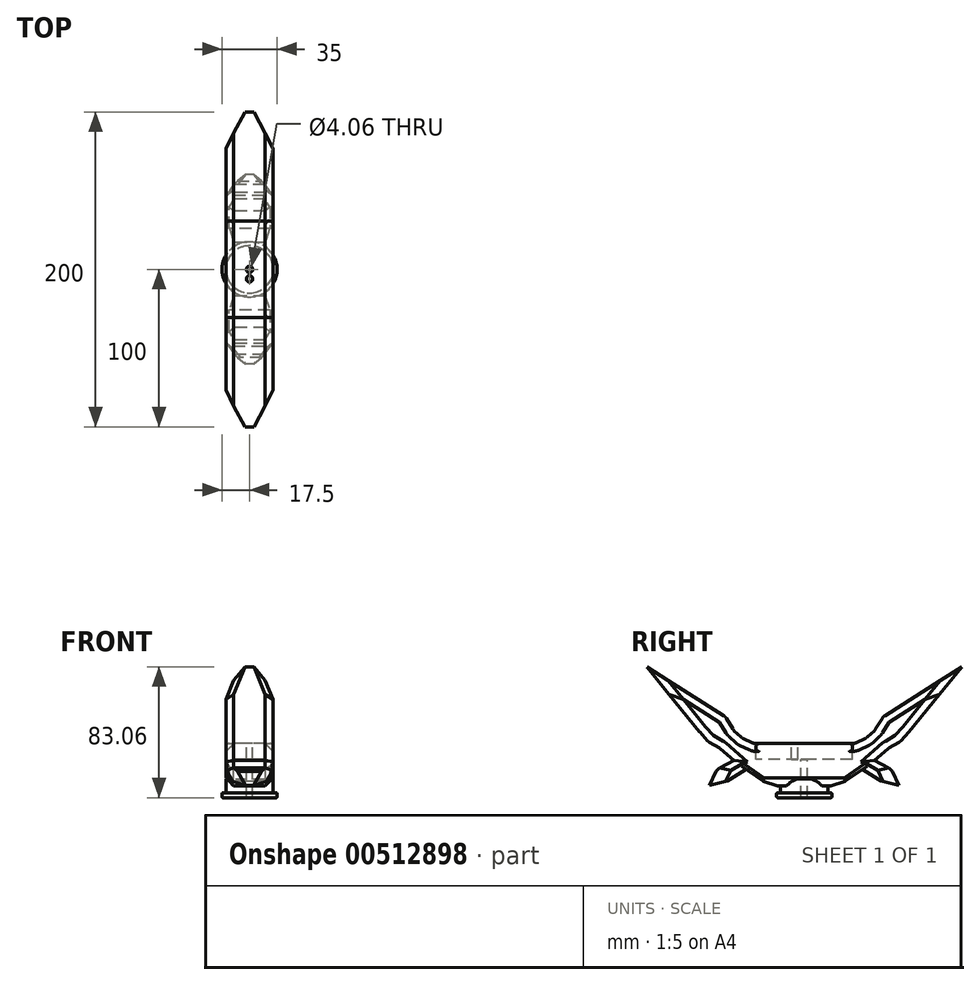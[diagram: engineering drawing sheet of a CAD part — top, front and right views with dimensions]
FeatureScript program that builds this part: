
annotation { "Feature Type Name" : "Feature", "Feature Type Description" : "" }
export const myFeature = defineFeature(function(context is Context, id is Id, definition is map)
    precondition{}
    {
        {
            var Q0;
            Q0=qCreatedBy(makeId("Right.planeOp"),FACE);
            var sketch = newSketch(context, id + "F0", { "sketchPlane" : qUnion([Q0])});
            skLineSegment(sketch, "E0", {"start": v(0, 19.85) * mm, "end": v(-31.76, 19.85) * mm});
            skLineSegment(sketch, "E1", {"start": v(-31.76, 19.85) * mm, "end": v(-39.55, 23.53) * mm});
            skLineSegment(sketch, "E2", {"start": v(-39.55, 23.53) * mm, "end": v(-45, 28.53) * mm});
            skLineSegment(sketch, "E3", {"start": v(-45, 28.53) * mm, "end": v(-50.14, 36.91) * mm});
            skLineSegment(sketch, "E4", {"start": v(-50.14, 36.91) * mm, "end": v(-100, 68.57) * mm});
            skLineSegment(sketch, "E5", {"start": v(-100, 68.57) * mm, "end": v(-66.42, 27.3) * mm});
            skLineSegment(sketch, "E6", {"start": v(-66.42, 27.3) * mm, "end": v(-60.82, 21) * mm});
            skLineSegment(sketch, "E7", {"start": v(-60.82, 21) * mm, "end": v(-53.48, 16.8) * mm});
            skLineSegment(sketch, "E8", {"start": v(-53.48, 16.8) * mm, "end": v(-44.73, 9.1) * mm});
            skLineSegment(sketch, "E9", {"start": v(-44.73, 9.1) * mm, "end": v(-55.22, 3.5) * mm});
            skLineSegment(sketch, "E10", {"start": v(-55.22, 3.5) * mm, "end": v(-60.12, -6.64) * mm});
            skLineSegment(sketch, "E11", {"start": v(-60.12, -6.64) * mm, "end": v(-47.88, -3.5) * mm});
            skLineSegment(sketch, "E12", {"start": v(-47.88, -3.5) * mm, "end": v(-37.03, 3.5) * mm});
            skLineSegment(sketch, "E13", {"start": v(-37.03, 3.5) * mm, "end": v(-25.84, -4.2) * mm});
            skLineSegment(sketch, "E14", {"start": v(-25.84, -4.2) * mm, "end": v(-17.1, -7) * mm});
            skLineSegment(sketch, "E15", {"start": v(-17.1, -7) * mm, "end": v(0, -7) * mm});
            skLineSegment(sketch, "E16.MirrorCS", {"start": v(0, 19.85) * mm, "end": v(31.76, 19.85) * mm});
            skLineSegment(sketch, "E17.MirrorCS", {"start": v(17.1, -7) * mm, "end": v(0, -7) * mm});
            skLineSegment(sketch, "E18.MirrorCS", {"start": v(25.84, -4.2) * mm, "end": v(17.1, -7) * mm});
            skLineSegment(sketch, "E19.MirrorCS", {"start": v(37.03, 3.5) * mm, "end": v(25.84, -4.2) * mm});
            skLineSegment(sketch, "E20.MirrorCS", {"start": v(47.88, -3.5) * mm, "end": v(37.03, 3.5) * mm});
            skLineSegment(sketch, "E21.MirrorCS", {"start": v(60.12, -6.64) * mm, "end": v(47.88, -3.5) * mm});
            skLineSegment(sketch, "E22.MirrorCS", {"start": v(55.22, 3.5) * mm, "end": v(60.12, -6.64) * mm});
            skLineSegment(sketch, "E23.MirrorCS", {"start": v(44.73, 9.1) * mm, "end": v(55.22, 3.5) * mm});
            skLineSegment(sketch, "E24.MirrorCS", {"start": v(53.48, 16.8) * mm, "end": v(44.73, 9.1) * mm});
            skLineSegment(sketch, "E25.MirrorCS", {"start": v(60.82, 21) * mm, "end": v(53.48, 16.8) * mm});
            skLineSegment(sketch, "E26.MirrorCS", {"start": v(66.42, 27.3) * mm, "end": v(60.82, 21) * mm});
            skLineSegment(sketch, "E27.MirrorCS", {"start": v(100, 68.57) * mm, "end": v(66.42, 27.3) * mm});
            skLineSegment(sketch, "E28.MirrorCS", {"start": v(50.14, 36.91) * mm, "end": v(100, 68.57) * mm});
            skLineSegment(sketch, "E29.MirrorCS", {"start": v(45, 28.53) * mm, "end": v(50.14, 36.91) * mm});
            skLineSegment(sketch, "E30.MirrorCS", {"start": v(39.55, 23.53) * mm, "end": v(45, 28.53) * mm});
            skLineSegment(sketch, "E31.MirrorCS", {"start": v(31.76, 19.85) * mm, "end": v(39.55, 23.53) * mm});
            skSolve(sketch);
        }
        {
            var Q0;
            Q0=makeQuery(id+"F0.imprint","IMPRINT",FACE,{"disambiguationData":[TD([[makeQuery(id+"F0.imprint","IMPRINT",EDGE,{"derivedFrom":sQuery(id+"F0.wireOp",EDGE,"E0")}),1.0]])]});
            extrude(context, id + "F1", {"entities" : qUnion([Q0]), "depth" : 30 * mm});
        }
        {
            var Q0;
            Q0=makeQuery(id+"F1.opExtrude","SWEPT_EDGE",EDGE,{"disambiguationData":[OSD([sQuery(id+"F0.wireOp",EDGE,"E7"),sQuery(id+"F0.wireOp",EDGE,"E8")])]});
            var Q1;
            Q1=makeQuery(id+"F1.opExtrude","SWEPT_EDGE",EDGE,{"disambiguationData":[OSD([sQuery(id+"F0.wireOp",EDGE,"E6"),sQuery(id+"F0.wireOp",EDGE,"E7")])]});
            var Q2;
            Q2=makeQuery(id+"F1.opExtrude","SWEPT_EDGE",EDGE,{"disambiguationData":[OSD([sQuery(id+"F0.wireOp",EDGE,"E5"),sQuery(id+"F0.wireOp",EDGE,"E6")])]});
            var Q3;
            Q3=makeQuery(id+"F1.opExtrude","SWEPT_EDGE",EDGE,{"disambiguationData":[OSD([sQuery(id+"F0.wireOp",EDGE,"E24.MirrorCS"),sQuery(id+"F0.wireOp",EDGE,"E25.MirrorCS")])]});
            var Q4;
            Q4=makeQuery(id+"F1.opExtrude","SWEPT_EDGE",EDGE,{"disambiguationData":[OSD([sQuery(id+"F0.wireOp",EDGE,"E25.MirrorCS"),sQuery(id+"F0.wireOp",EDGE,"E26.MirrorCS")])]});
            var Q5;
            Q5=makeQuery(id+"F1.opExtrude","SWEPT_EDGE",EDGE,{"disambiguationData":[OSD([sQuery(id+"F0.wireOp",EDGE,"E26.MirrorCS"),sQuery(id+"F0.wireOp",EDGE,"E27.MirrorCS")])]});
            var Q6;
            Q6=makeQuery(id+"F1.opExtrude","SWEPT_EDGE",EDGE,{"disambiguationData":[OSD([sQuery(id+"F0.wireOp",EDGE,"E28.MirrorCS"),sQuery(id+"F0.wireOp",EDGE,"E29.MirrorCS")])]});
            var Q7;
            Q7=makeQuery(id+"F1.opExtrude","SWEPT_EDGE",EDGE,{"disambiguationData":[OSD([sQuery(id+"F0.wireOp",EDGE,"E29.MirrorCS"),sQuery(id+"F0.wireOp",EDGE,"E30.MirrorCS")])]});
            var Q8;
            Q8=makeQuery(id+"F1.opExtrude","SWEPT_EDGE",EDGE,{"disambiguationData":[OSD([sQuery(id+"F0.wireOp",EDGE,"E30.MirrorCS"),sQuery(id+"F0.wireOp",EDGE,"E31.MirrorCS")])]});
            var Q9;
            Q9=makeQuery(id+"F1.opExtrude","SWEPT_EDGE",EDGE,{"disambiguationData":[OSD([sQuery(id+"F0.wireOp",EDGE,"E16.MirrorCS"),sQuery(id+"F0.wireOp",EDGE,"E31.MirrorCS")])]});
            var Q10;
            Q10=makeQuery(id+"F1.opExtrude","SWEPT_EDGE",EDGE,{"disambiguationData":[OSD([sQuery(id+"F0.wireOp",EDGE,"E0"),sQuery(id+"F0.wireOp",EDGE,"E1")])]});
            var Q11;
            Q11=makeQuery(id+"F1.opExtrude","SWEPT_EDGE",EDGE,{"disambiguationData":[OSD([sQuery(id+"F0.wireOp",EDGE,"E1"),sQuery(id+"F0.wireOp",EDGE,"E2")])]});
            var Q12;
            Q12=makeQuery(id+"F1.opExtrude","SWEPT_EDGE",EDGE,{"disambiguationData":[OSD([sQuery(id+"F0.wireOp",EDGE,"E2"),sQuery(id+"F0.wireOp",EDGE,"E3")])]});
            var Q13;
            Q13=makeQuery(id+"F1.opExtrude","SWEPT_EDGE",EDGE,{"disambiguationData":[OSD([sQuery(id+"F0.wireOp",EDGE,"E3"),sQuery(id+"F0.wireOp",EDGE,"E4")])]});
            fillet(context, id + "F2", {"entities" : qUnion([Q0, Q1, Q2, Q3, Q4, Q5, Q6, Q7, Q8, Q9, Q10, Q11, Q12, Q13]), "radius" : 5 * mm, "tangentPropagation" : true, "allowEdgeOverflow" : false});
        }
        {
            var Q0;
            Q0=makeQuery(id+"F1.opExtrude","SWEPT_EDGE",EDGE,{"disambiguationData":[OSD([sQuery(id+"F0.wireOp",EDGE,"E9"),sQuery(id+"F0.wireOp",EDGE,"E10")])]});
            var Q1;
            Q1=makeQuery(id+"F1.opExtrude","SWEPT_EDGE",EDGE,{"disambiguationData":[OSD([sQuery(id+"F0.wireOp",EDGE,"E11"),sQuery(id+"F0.wireOp",EDGE,"E12")])]});
            var Q2;
            Q2=makeQuery(id+"F1.opExtrude","SWEPT_EDGE",EDGE,{"disambiguationData":[OSD([sQuery(id+"F0.wireOp",EDGE,"E22.MirrorCS"),sQuery(id+"F0.wireOp",EDGE,"E23.MirrorCS")])]});
            var Q3;
            Q3=makeQuery(id+"F1.opExtrude","SWEPT_EDGE",EDGE,{"disambiguationData":[OSD([sQuery(id+"F0.wireOp",EDGE,"E20.MirrorCS"),sQuery(id+"F0.wireOp",EDGE,"E21.MirrorCS")])]});
            chamfer(context, id + "F3", {"entities" : qUnion([Q0, Q1, Q2, Q3]), "width" : 5 * mm, "tangentPropagation" : true});
        }
        {
            var Q0;
            Q0=makeQuery(id+"F1.opExtrude","CAP_EDGE",EDGE,{"disambiguationData":[OSD([sQuery(id+"F0.wireOp",EDGE,"E4")])],"isStart":false});
            var Q1;
            Q1=makeQuery(id+"F1.opExtrude","CAP_EDGE",EDGE,{"disambiguationData":[OSD([sQuery(id+"F0.wireOp",EDGE,"E4")])],"isStart":true});
            var Q2;
            Q2=makeQuery(id+"F1.opExtrude","CAP_EDGE",EDGE,{"disambiguationData":[OSD([sQuery(id+"F0.wireOp",EDGE,"E15"),sQuery(id+"F0.wireOp",EDGE,"E17.MirrorCS")])],"isStart":false});
            var Q3;
            Q3=makeQuery(id+"F1.opExtrude","CAP_EDGE",EDGE,{"disambiguationData":[OSD([sQuery(id+"F0.wireOp",EDGE,"E15"),sQuery(id+"F0.wireOp",EDGE,"E17.MirrorCS")])],"isStart":true});
            chamfer(context, id + "F4", {"entities" : qUnion([Q0, Q1, Q2, Q3]), "width" : 5 * mm, "tangentPropagation" : true});
        }
        {
            var Q0;
            Q0=makeQuery(id+"F4.opChamfer","BLEND_EDGE",EDGE,{"blendedFrom":[makeQuery(id+"F1.opExtrude","CAP_EDGE",EDGE,{"disambiguationData":[OSD([sQuery(id+"F0.wireOp",EDGE,"E4")])],"isStart":false}),makeQuery(id+"F1.opExtrude","SWEPT_FACE",FACE,{"disambiguationData":[OSD([sQuery(id+"F0.wireOp",EDGE,"E5")])]})],"blendedInto":[makeQuery(id+"F1.opExtrude","SWEPT_FACE",FACE,{"disambiguationData":[OSD([sQuery(id+"F0.wireOp",EDGE,"E5")])]})]});
            var Q1;
            Q1=makeQuery(id+"F4.opChamfer","BLEND_EDGE",EDGE,{"blendedFrom":[makeQuery(id+"F1.opExtrude","CAP_EDGE",EDGE,{"disambiguationData":[OSD([sQuery(id+"F0.wireOp",EDGE,"E4")])],"isStart":true}),makeQuery(id+"F1.opExtrude","SWEPT_FACE",FACE,{"disambiguationData":[OSD([sQuery(id+"F0.wireOp",EDGE,"E5")])]})],"blendedInto":[makeQuery(id+"F1.opExtrude","SWEPT_FACE",FACE,{"disambiguationData":[OSD([sQuery(id+"F0.wireOp",EDGE,"E5")])]})]});
            var Q2;
            Q2=makeQuery(id+"F4.opChamfer","BLEND_EDGE",EDGE,{"blendedFrom":[makeQuery(id+"F1.opExtrude","CAP_EDGE",EDGE,{"disambiguationData":[OSD([sQuery(id+"F0.wireOp",EDGE,"E28.MirrorCS")])],"isStart":true}),makeQuery(id+"F1.opExtrude","SWEPT_FACE",FACE,{"disambiguationData":[OSD([sQuery(id+"F0.wireOp",EDGE,"E27.MirrorCS")])]})],"blendedInto":[makeQuery(id+"F1.opExtrude","SWEPT_FACE",FACE,{"disambiguationData":[OSD([sQuery(id+"F0.wireOp",EDGE,"E27.MirrorCS")])]})]});
            var Q3;
            Q3=makeQuery(id+"F4.opChamfer","BLEND_EDGE",EDGE,{"blendedFrom":[makeQuery(id+"F1.opExtrude","CAP_EDGE",EDGE,{"disambiguationData":[OSD([sQuery(id+"F0.wireOp",EDGE,"E28.MirrorCS")])],"isStart":false}),makeQuery(id+"F1.opExtrude","SWEPT_FACE",FACE,{"disambiguationData":[OSD([sQuery(id+"F0.wireOp",EDGE,"E27.MirrorCS")])]})],"blendedInto":[makeQuery(id+"F1.opExtrude","SWEPT_FACE",FACE,{"disambiguationData":[OSD([sQuery(id+"F0.wireOp",EDGE,"E27.MirrorCS")])]})]});
            chamfer(context, id + "F5", {"entities" : qUnion([Q0, Q1, Q2, Q3]), "width" : 3 * mm, "tangentPropagation" : true});
        }
        {
            var Q0;
            Q0=makeQuery(id+"F1.opExtrude","SWEPT_FACE",FACE,{"disambiguationData":[OSD([sQuery(id+"F0.wireOp",EDGE,"E0"),sQuery(id+"F0.wireOp",EDGE,"E16.MirrorCS")])]});
            var sketch = newSketch(context, id + "F6", { "sketchPlane" : qUnion([Q0])});
            skLineSegment(sketch, "E32", {"start": v(0, 30.64) * mm, "end": v(30, 30.64) * mm});
            skLineSegment(sketch, "E33", {"start": v(0, -30.64) * mm, "end": v(30, -30.64) * mm});
            skPoint(sketch, "E33.endSnap0", {"position": v(15, -30.64) * mm});
            skLineSegment(sketch, "E34", {"start": v(30, 30.64) * mm, "end": v(30, -30.64) * mm});
            skLineSegment(sketch, "E35", {"start": v(0, 30.64) * mm, "end": v(0, -30.64) * mm});
            skCircle(sketch, "E36", {"center": v(15, 6.02) * mm, "radius": 2.03 * mm});
            skCircle(sketch, "E37.MirrorC", {"center": v(15, -6.02) * mm, "radius": 2.03 * mm});
            skSolve(sketch);
        }
        {
            var Q0;
            Q0 = qSketchRegion(id + "F6", true);
            extrude(context, id + "F7", {"entities" : qUnion([Q0]), "operationType" : NewBodyOperationType.ADD, "oppositeDirection" : true, "depth" : 5 * mm});
        }
        {
            var Q0;
            {var subQ33=sQuery(id+"F6.wireOp",EDGE,"E34");var subQ34=sQuery(id+"F6.wireOp",EDGE,"E33");Q0=makeQuery(id+"F7.boolean.opBoolean","SPLIT",EDGE,{"disambiguationData":[TD([makeQuery(id+"F7.opExtrude","SWEPT_FACE",FACE,{"disambiguationData":[OSD([subQ33])]})])],"derivedFrom":makeQuery(id+"F7.opExtrude","CAP_EDGE",EDGE,{"disambiguationData":[OSD([subQ34])],"isStart":true})});}
            var Q1;
            Q1=makeQuery(id+"F7.opExtrude","SWEPT_EDGE",EDGE,{"disambiguationData":[OSD([sQuery(id+"F6.wireOp",EDGE,"E33"),sQuery(id+"F6.wireOp",EDGE,"E34")])]});
            var Q2;
            {var subQ33=sQuery(id+"F6.wireOp",EDGE,"E35");var subQ34=sQuery(id+"F6.wireOp",EDGE,"E33");Q2=makeQuery(id+"F7.boolean.opBoolean","SPLIT",EDGE,{"disambiguationData":[TD([makeQuery(id+"F7.opExtrude","SWEPT_FACE",FACE,{"disambiguationData":[OSD([subQ33])]})])],"derivedFrom":makeQuery(id+"F7.opExtrude","CAP_EDGE",EDGE,{"disambiguationData":[OSD([subQ34])],"isStart":true})});}
            var Q3;
            Q3=makeQuery(id+"F7.opExtrude","SWEPT_EDGE",EDGE,{"disambiguationData":[OSD([sQuery(id+"F6.wireOp",EDGE,"E33"),sQuery(id+"F6.wireOp",EDGE,"E35")])]});
            var Q4;
            Q4=makeQuery(id+"F7.opExtrude","SWEPT_EDGE",EDGE,{"disambiguationData":[OSD([sQuery(id+"F6.wireOp",EDGE,"E32"),sQuery(id+"F6.wireOp",EDGE,"E35")])]});
            var Q5;
            {var subQ33=sQuery(id+"F6.wireOp",EDGE,"E35");var subQ34=sQuery(id+"F6.wireOp",EDGE,"E32");Q5=makeQuery(id+"F7.boolean.opBoolean","SPLIT",EDGE,{"disambiguationData":[TD([makeQuery(id+"F7.opExtrude","SWEPT_FACE",FACE,{"disambiguationData":[OSD([subQ33])]})])],"derivedFrom":makeQuery(id+"F7.opExtrude","CAP_EDGE",EDGE,{"disambiguationData":[OSD([subQ34])],"isStart":true})});}
            var Q6;
            Q6=makeQuery(id+"F7.opExtrude","SWEPT_EDGE",EDGE,{"disambiguationData":[OSD([sQuery(id+"F6.wireOp",EDGE,"E32"),sQuery(id+"F6.wireOp",EDGE,"E34")])]});
            var Q7;
            {var subQ33=sQuery(id+"F6.wireOp",EDGE,"E32");var subQ34=sQuery(id+"F6.wireOp",EDGE,"E34");Q7=makeQuery(id+"F7.boolean.opBoolean","SPLIT",EDGE,{"disambiguationData":[TD([makeQuery(id+"F7.opExtrude","SWEPT_FACE",FACE,{"disambiguationData":[OSD([subQ34])]})])],"derivedFrom":makeQuery(id+"F7.opExtrude","CAP_EDGE",EDGE,{"disambiguationData":[OSD([subQ33])],"isStart":true})});}
            fillet(context, id + "F8", {"entities" : qUnion([Q0, Q1, Q2, Q3, Q4, Q5, Q6, Q7]), "radius" : 2 * mm, "tangentPropagation" : true, "allowEdgeOverflow" : false});
        }
        {
            var Q0;
            Q0=makeQuery(id+"F1.opExtrude","SWEPT_FACE",FACE,{"disambiguationData":[OSD([sQuery(id+"F0.wireOp",EDGE,"E15"),sQuery(id+"F0.wireOp",EDGE,"E17.MirrorCS")])]});
            var sketch = newSketch(context, id + "F9", { "sketchPlane" : qUnion([Q0])});
            skCircle(sketch, "E38", {"center": v(15, 0) * mm, "radius": 15 * mm});
            skPoint(sketch, "E38.centerSnap0", {"position": v(15, 17.1) * mm});
            skSolve(sketch);
        }
        {
            var Q0;
            Q0 = qSketchRegion(id + "F9", true);
            extrude(context, id + "F10", {"entities" : qUnion([Q0]), "operationType" : NewBodyOperationType.ADD, "endBound" : BoundingType.SYMMETRIC, "oppositeDirection" : true, "depth" : 9 * mm});
        }
        {
            var Q0;
            Q0=makeQuery(id+"F10.opExtrude","CAP_FACE",FACE,{"disambiguationData":[OSD([sQuery(id+"F9.wireOp",EDGE,"E38")])],"isStart":true});
            var sketch = newSketch(context, id + "F11", { "sketchPlane" : qUnion([Q0])});
            skCircle(sketch, "E39", {"center": v(15, 0) * mm, "radius": 17.5 * mm});
            skCircle(sketch, "E40", {"center": v(15, 0) * mm, "radius": 2.03 * mm});
            skSolve(sketch);
        }
        {
            var Q0;
            Q0 = qSketchRegion(id + "F11", true);
            extrude(context, id + "F12", {"entities" : qUnion([Q0]), "operationType" : NewBodyOperationType.ADD, "depth" : 3 * mm, "offsetDistance" : 25 * mm});
        }
        {
            var Q0;
            Q0=makeQuery(id+"F12.opExtrude","CAP_EDGE",EDGE,{"disambiguationData":[OSD([sQuery(id+"F11.wireOp",EDGE,"E39")])],"isStart":true});
            var Q1;
            Q1=makeQuery(id+"F12.opExtrude","CAP_EDGE",EDGE,{"disambiguationData":[OSD([sQuery(id+"F11.wireOp",EDGE,"E39")])],"isStart":false});
            fillet(context, id + "F13", {"entities" : qUnion([Q0, Q1]), "radius" : .5 * mm, "tangentPropagation" : true, "allowEdgeOverflow" : false});
        }
        {
            var Q0;
            Q0=makeQuery(id+"F7.opExtrude","CAP_EDGE",EDGE,{"disambiguationData":[OSD([sQuery(id+"F6.wireOp",EDGE,"E34")])],"isStart":true});
            var Q1;
            Q1=makeQuery(id+"F7.opExtrude","CAP_EDGE",EDGE,{"disambiguationData":[OSD([sQuery(id+"F6.wireOp",EDGE,"E35")])],"isStart":true});
            fillet(context, id + "F14", {"entities" : qUnion([Q0, Q1]), "radius" : 2 * mm, "tangentPropagation" : true, "allowEdgeOverflow" : false});
        }
        {
            var Q0;
            {var subQ0=sQuery(id+"F6.wireOp",EDGE,"E37.MirrorC");var subQ1=sQuery(id+"F0.wireOp",EDGE,"E16.MirrorCS");var subQ2=sQuery(id+"F0.wireOp",EDGE,"E0");var subQ3=makeQuery(id+"F1.opExtrude","SWEPT_FACE",FACE,{"disambiguationData":[OSD([subQ2,subQ1])]});var subQ4=makeQuery(id+"F4.opChamfer","BLEND_EDGE",EDGE,{"blendedFrom":[makeQuery(id+"F1.opExtrude","CAP_EDGE",EDGE,{"disambiguationData":[OSD([subQ2,subQ1])],"isStart":true}),subQ3],"blendedInto":[subQ3]});var subQ5=makeQuery(id+"F6.imprint","INTERSECT",VERTEX,{"disambiguationData":[OD(0.0)],"derivedFrom":[subQ4,subQ0]});Q0=makeQuery(id+"F6.imprint","IMPRINT",FACE,{"disambiguationData":[TD([[makeQuery(id+"F6.imprint","IMPRINT",EDGE,{"disambiguationData":[TD([[subQ5,1.0]])],"derivedFrom":subQ0}),-1.0]])]});}
            var Q1;
            {var subQ0=sQuery(id+"F6.wireOp",EDGE,"E36");var subQ1=sQuery(id+"F0.wireOp",EDGE,"E16.MirrorCS");var subQ2=sQuery(id+"F0.wireOp",EDGE,"E0");var subQ3=makeQuery(id+"F1.opExtrude","SWEPT_FACE",FACE,{"disambiguationData":[OSD([subQ2,subQ1])]});var subQ4=makeQuery(id+"F4.opChamfer","BLEND_EDGE",EDGE,{"blendedFrom":[makeQuery(id+"F1.opExtrude","CAP_EDGE",EDGE,{"disambiguationData":[OSD([subQ2,subQ1])],"isStart":true}),subQ3],"blendedInto":[subQ3]});var subQ5=makeQuery(id+"F6.imprint","INTERSECT",VERTEX,{"disambiguationData":[OD(0.0)],"derivedFrom":[subQ4,subQ0]});Q1=makeQuery(id+"F6.imprint","IMPRINT",FACE,{"disambiguationData":[TD([[makeQuery(id+"F6.imprint","IMPRINT",EDGE,{"disambiguationData":[TD([[subQ5,1.0]])],"derivedFrom":subQ0}),1.0]])]});}
            var Q2;
            {var subQ0=sQuery(id+"F6.wireOp",EDGE,"E36");var subQ1=sQuery(id+"F0.wireOp",EDGE,"E16.MirrorCS");var subQ2=sQuery(id+"F0.wireOp",EDGE,"E0");var subQ3=makeQuery(id+"F4.opChamfer","BLEND_EDGE",EDGE,{"blendedFrom":[makeQuery(id+"F1.opExtrude","CAP_EDGE",EDGE,{"disambiguationData":[OSD([subQ2,subQ1])],"isStart":false}),makeQuery(id+"F1.opExtrude","SWEPT_FACE",FACE,{"disambiguationData":[OSD([subQ2,subQ1])]})],"blendedInto":[makeQuery(id+"F1.opExtrude","SWEPT_FACE",FACE,{"disambiguationData":[OSD([subQ2,subQ1])]})]});var subQ4=makeQuery(id+"F6.imprint","INTERSECT",VERTEX,{"disambiguationData":[OD(0.0)],"derivedFrom":[subQ3,subQ0]});Q2=makeQuery(id+"F6.imprint","IMPRINT",FACE,{"disambiguationData":[TD([[makeQuery(id+"F6.imprint","IMPRINT",EDGE,{"disambiguationData":[TD([[subQ4,1.0]])],"derivedFrom":subQ0}),1.0]])]});}
            var Q3;
            {var subQ0=sQuery(id+"F6.wireOp",EDGE,"E36");var subQ1=sQuery(id+"F0.wireOp",EDGE,"E16.MirrorCS");var subQ2=sQuery(id+"F0.wireOp",EDGE,"E0");var subQ3=makeQuery(id+"F4.opChamfer","BLEND_EDGE",EDGE,{"blendedFrom":[makeQuery(id+"F1.opExtrude","CAP_EDGE",EDGE,{"disambiguationData":[OSD([subQ2,subQ1])],"isStart":true}),makeQuery(id+"F1.opExtrude","SWEPT_FACE",FACE,{"disambiguationData":[OSD([subQ2,subQ1])]})],"blendedInto":[makeQuery(id+"F1.opExtrude","SWEPT_FACE",FACE,{"disambiguationData":[OSD([subQ2,subQ1])]})]});var subQ4=makeQuery(id+"F6.imprint","INTERSECT",VERTEX,{"disambiguationData":[OD(0.0)],"derivedFrom":[subQ3,subQ0]});Q3=makeQuery(id+"F6.imprint","IMPRINT",FACE,{"disambiguationData":[TD([[makeQuery(id+"F6.imprint","IMPRINT",EDGE,{"disambiguationData":[TD([[subQ4,-1.0]])],"derivedFrom":subQ0}),1.0]])]});}
            var Q4;
            {var subQ0=sQuery(id+"F6.wireOp",EDGE,"E37.MirrorC");var subQ1=sQuery(id+"F0.wireOp",EDGE,"E16.MirrorCS");var subQ2=sQuery(id+"F0.wireOp",EDGE,"E0");var subQ3=makeQuery(id+"F4.opChamfer","BLEND_EDGE",EDGE,{"blendedFrom":[makeQuery(id+"F1.opExtrude","CAP_EDGE",EDGE,{"disambiguationData":[OSD([subQ2,subQ1])],"isStart":false}),makeQuery(id+"F1.opExtrude","SWEPT_FACE",FACE,{"disambiguationData":[OSD([subQ2,subQ1])]})],"blendedInto":[makeQuery(id+"F1.opExtrude","SWEPT_FACE",FACE,{"disambiguationData":[OSD([subQ2,subQ1])]})]});var subQ4=makeQuery(id+"F6.imprint","INTERSECT",VERTEX,{"disambiguationData":[OD(0.0)],"derivedFrom":[subQ3,subQ0]});Q4=makeQuery(id+"F6.imprint","IMPRINT",FACE,{"disambiguationData":[TD([[makeQuery(id+"F6.imprint","IMPRINT",EDGE,{"disambiguationData":[TD([[subQ4,1.0]])],"derivedFrom":subQ0}),-1.0]])]});}
            var Q5;
            {var subQ0=sQuery(id+"F6.wireOp",EDGE,"E37.MirrorC");var subQ1=sQuery(id+"F0.wireOp",EDGE,"E16.MirrorCS");var subQ2=sQuery(id+"F0.wireOp",EDGE,"E0");var subQ3=makeQuery(id+"F4.opChamfer","BLEND_EDGE",EDGE,{"blendedFrom":[makeQuery(id+"F1.opExtrude","CAP_EDGE",EDGE,{"disambiguationData":[OSD([subQ2,subQ1])],"isStart":true}),makeQuery(id+"F1.opExtrude","SWEPT_FACE",FACE,{"disambiguationData":[OSD([subQ2,subQ1])]})],"blendedInto":[makeQuery(id+"F1.opExtrude","SWEPT_FACE",FACE,{"disambiguationData":[OSD([subQ2,subQ1])]})]});var subQ4=makeQuery(id+"F6.imprint","INTERSECT",VERTEX,{"disambiguationData":[OD(0.0)],"derivedFrom":[subQ3,subQ0]});Q5=makeQuery(id+"F6.imprint","IMPRINT",FACE,{"disambiguationData":[TD([[makeQuery(id+"F6.imprint","IMPRINT",EDGE,{"disambiguationData":[TD([[subQ4,-1.0]])],"derivedFrom":subQ0}),-1.0]])]});}
            extrude(context, id + "F15", {"entities" : qUnion([Q0, Q1, Q2, Q3, Q4, Q5]), "operationType" : NewBodyOperationType.REMOVE, "oppositeDirection" : true, "depth" : 10 * mm});
        }
        {
            var Q0;
            Q0=makeQuery(id+"F1.opExtrude","CAP_EDGE",EDGE,{"disambiguationData":[OSD([sQuery(id+"F0.wireOp",EDGE,"E27.MirrorCS")])],"isStart":true});
            var Q1;
            Q1=makeQuery(id+"F1.opExtrude","CAP_EDGE",EDGE,{"disambiguationData":[OSD([sQuery(id+"F0.wireOp",EDGE,"E27.MirrorCS")])],"isStart":false});
            var Q2;
            Q2=makeQuery(id+"F1.opExtrude","CAP_EDGE",EDGE,{"disambiguationData":[OSD([sQuery(id+"F0.wireOp",EDGE,"E5")])],"isStart":false});
            var Q3;
            Q3=makeQuery(id+"F1.opExtrude","CAP_EDGE",EDGE,{"disambiguationData":[OSD([sQuery(id+"F0.wireOp",EDGE,"E5")])],"isStart":true});
            chamfer(context, id + "F16", {"entities" : qUnion([Q0, Q1, Q2, Q3]), "width" : 5 * mm, "tangentPropagation" : true});
        }
        {
            var Q0;
            Q0=makeQuery(id+"F1.opExtrude","CAP_EDGE",EDGE,{"disambiguationData":[OSD([sQuery(id+"F0.wireOp",EDGE,"E23.MirrorCS")])],"isStart":true});
            var Q1;
            Q1=makeQuery(id+"F1.opExtrude","CAP_EDGE",EDGE,{"disambiguationData":[OSD([sQuery(id+"F0.wireOp",EDGE,"E23.MirrorCS")])],"isStart":false});
            var Q2;
            Q2=makeQuery(id+"F1.opExtrude","CAP_EDGE",EDGE,{"disambiguationData":[OSD([sQuery(id+"F0.wireOp",EDGE,"E9")])],"isStart":true});
            var Q3;
            Q3=makeQuery(id+"F1.opExtrude","CAP_EDGE",EDGE,{"disambiguationData":[OSD([sQuery(id+"F0.wireOp",EDGE,"E9")])],"isStart":false});
            var Q4;
            Q4=makeQuery(id+"F1.opExtrude","CAP_EDGE",EDGE,{"disambiguationData":[OSD([sQuery(id+"F0.wireOp",EDGE,"E12")])],"isStart":false});
            var Q5;
            Q5=makeQuery(id+"F1.opExtrude","CAP_EDGE",EDGE,{"disambiguationData":[OSD([sQuery(id+"F0.wireOp",EDGE,"E12")])],"isStart":true});
            var Q6;
            Q6=makeQuery(id+"F1.opExtrude","CAP_EDGE",EDGE,{"disambiguationData":[OSD([sQuery(id+"F0.wireOp",EDGE,"E20.MirrorCS")])],"isStart":true});
            var Q7;
            Q7=makeQuery(id+"F1.opExtrude","CAP_EDGE",EDGE,{"disambiguationData":[OSD([sQuery(id+"F0.wireOp",EDGE,"E20.MirrorCS")])],"isStart":false});
            chamfer(context, id + "F17", {"entities" : qUnion([Q0, Q1, Q2, Q3, Q4, Q5, Q6, Q7]), "width" : 5 * mm, "tangentPropagation" : true});
        }
        {
            var Q0;
            Q0=makeQuery(id+"F17.opChamfer","BLEND_EDGE",EDGE,{"blendedFrom":[makeQuery(id+"F1.opExtrude","CAP_EDGE",EDGE,{"disambiguationData":[OSD([sQuery(id+"F0.wireOp",EDGE,"E20.MirrorCS")])],"isStart":true}),makeQuery(id+"F1.opExtrude","SWEPT_FACE",FACE,{"disambiguationData":[OSD([sQuery(id+"F0.wireOp",EDGE,"E22.MirrorCS")])]})],"blendedInto":[makeQuery(id+"F1.opExtrude","SWEPT_FACE",FACE,{"disambiguationData":[OSD([sQuery(id+"F0.wireOp",EDGE,"E22.MirrorCS")])]})]});
            var Q1;
            Q1=makeQuery(id+"F17.opChamfer","BLEND_EDGE",EDGE,{"blendedFrom":[makeQuery(id+"F1.opExtrude","CAP_EDGE",EDGE,{"disambiguationData":[OSD([sQuery(id+"F0.wireOp",EDGE,"E20.MirrorCS")])],"isStart":false}),makeQuery(id+"F1.opExtrude","SWEPT_FACE",FACE,{"disambiguationData":[OSD([sQuery(id+"F0.wireOp",EDGE,"E22.MirrorCS")])]})],"blendedInto":[makeQuery(id+"F1.opExtrude","SWEPT_FACE",FACE,{"disambiguationData":[OSD([sQuery(id+"F0.wireOp",EDGE,"E22.MirrorCS")])]})]});
            var Q2;
            Q2=makeQuery(id+"F17.opChamfer","BLEND_EDGE",EDGE,{"blendedFrom":[makeQuery(id+"F1.opExtrude","CAP_EDGE",EDGE,{"disambiguationData":[OSD([sQuery(id+"F0.wireOp",EDGE,"E12")])],"isStart":true}),makeQuery(id+"F1.opExtrude","SWEPT_FACE",FACE,{"disambiguationData":[OSD([sQuery(id+"F0.wireOp",EDGE,"E10")])]})],"blendedInto":[makeQuery(id+"F1.opExtrude","SWEPT_FACE",FACE,{"disambiguationData":[OSD([sQuery(id+"F0.wireOp",EDGE,"E10")])]})]});
            var Q3;
            Q3=makeQuery(id+"F17.opChamfer","BLEND_EDGE",EDGE,{"blendedFrom":[makeQuery(id+"F1.opExtrude","CAP_EDGE",EDGE,{"disambiguationData":[OSD([sQuery(id+"F0.wireOp",EDGE,"E12")])],"isStart":false}),makeQuery(id+"F1.opExtrude","SWEPT_FACE",FACE,{"disambiguationData":[OSD([sQuery(id+"F0.wireOp",EDGE,"E10")])]})],"blendedInto":[makeQuery(id+"F1.opExtrude","SWEPT_FACE",FACE,{"disambiguationData":[OSD([sQuery(id+"F0.wireOp",EDGE,"E10")])]})]});
            chamfer(context, id + "F18", {"entities" : qUnion([Q0, Q1, Q2, Q3]), "width" : 5 * mm, "tangentPropagation" : true});
        }
        {
            var Q0;
            Q0=makeQuery(id+"F1.opExtrude","CAP_EDGE",EDGE,{"disambiguationData":[OSD([sQuery(id+"F0.wireOp",EDGE,"E19.MirrorCS")])],"isStart":true});
            var Q1;
            Q1=makeQuery(id+"F1.opExtrude","CAP_EDGE",EDGE,{"disambiguationData":[OSD([sQuery(id+"F0.wireOp",EDGE,"E19.MirrorCS")])],"isStart":false});
            var Q2;
            Q2=makeQuery(id+"F1.opExtrude","CAP_EDGE",EDGE,{"disambiguationData":[OSD([sQuery(id+"F0.wireOp",EDGE,"E13")])],"isStart":true});
            var Q3;
            Q3=makeQuery(id+"F1.opExtrude","CAP_EDGE",EDGE,{"disambiguationData":[OSD([sQuery(id+"F0.wireOp",EDGE,"E13")])],"isStart":false});
            chamfer(context, id + "F19", {"entities" : qUnion([Q0, Q1, Q2, Q3]), "width" : 2 * mm, "tangentPropagation" : true});
        }
        {
            var Q0;
            Q0=makeQuery(id+"F11.imprint","IMPRINT",FACE,{"disambiguationData":[TD([[makeQuery(id+"F11.imprint","IMPRINT",EDGE,{"derivedFrom":sQuery(id+"F11.wireOp",EDGE,"E40")}),1.0]])]});
            extrude(context, id + "F20", {"entities" : qUnion([Q0]), "operationType" : NewBodyOperationType.REMOVE, "oppositeDirection" : true, "depth" : 25 * mm});
        }
    });
